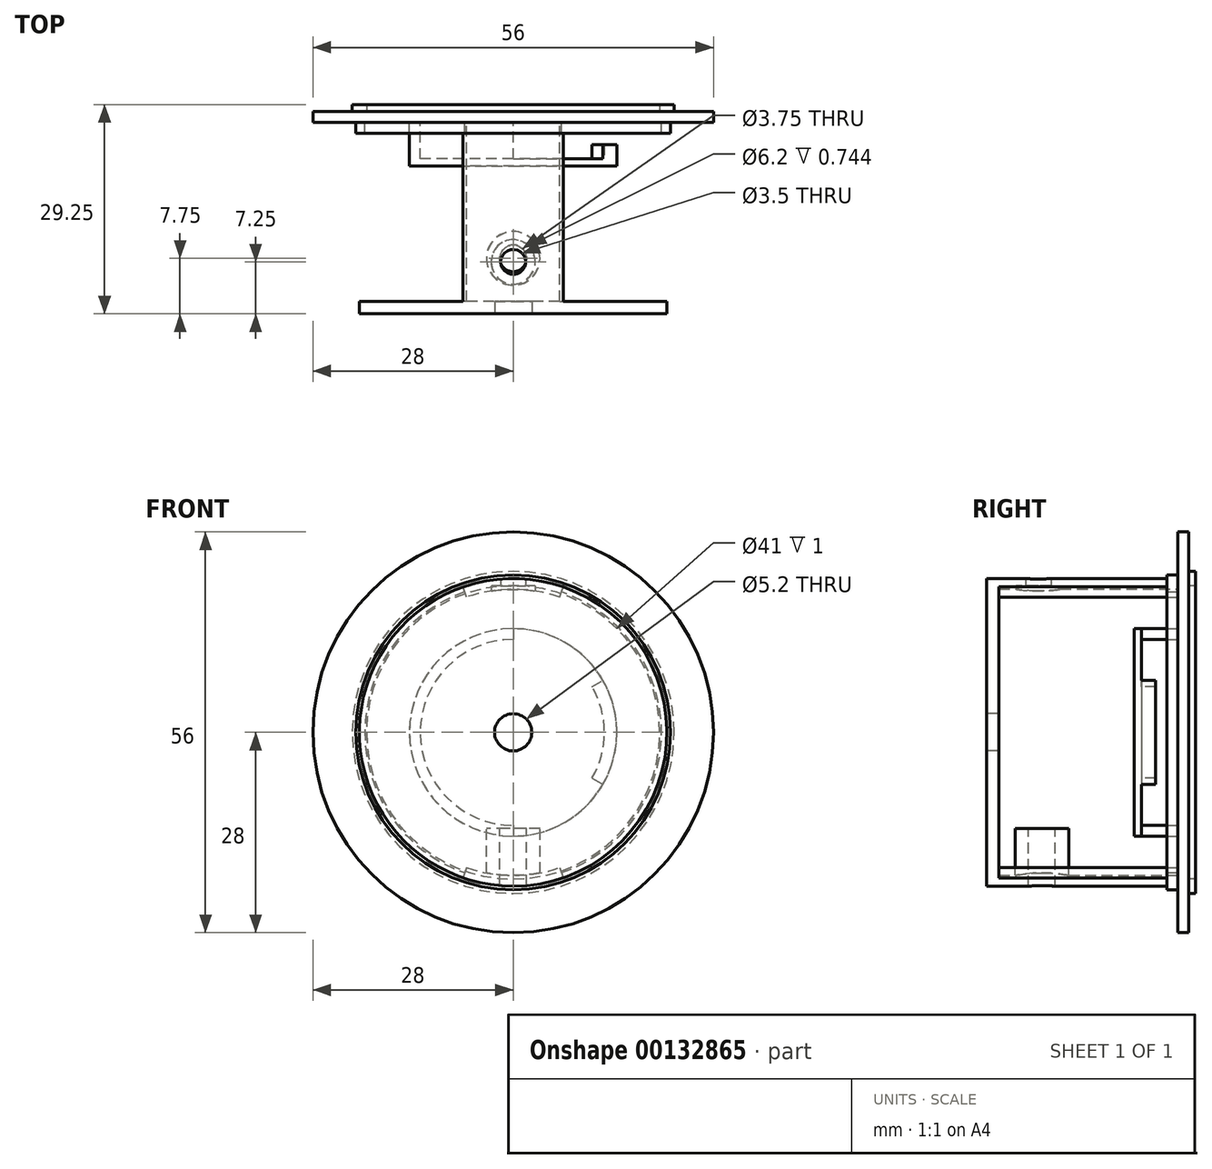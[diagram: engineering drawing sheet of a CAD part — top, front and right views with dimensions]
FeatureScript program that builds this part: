
annotation { "Feature Type Name" : "Feature", "Feature Type Description" : "" }
export const myFeature = defineFeature(function(context is Context, id is Id, definition is map)
    precondition{}
    {
        {
            var Q0;
            Q0=qCreatedBy(makeId("Front.planeOp"),FACE);
            var sketch = newSketch(context, id + "F0", { "sketchPlane" : qUnion([Q0])});
            skCircle(sketch, "E0", {"center": v(0, 0) * mm, "radius": 28 * mm});
            skSolve(sketch);
        }
        {
            var Q0;
            Q0=qSketchRegion(id+"F0",true);
            extrude(context, id + "F1", {"entities" : qUnion([Q0]), "depth" : 1.5 * mm});
        }
        {
            var Q0;
            Q0=makeQuery(id+"F1.opExtrude","CAP_FACE",FACE,{"disambiguationData":[OSD([sQuery(id+"F0.wireOp",EDGE,"E0")])],"isStart":false});
            var sketch = newSketch(context, id + "F2", { "sketchPlane" : qUnion([Q0])});
            skArc(sketch, "E1", {"start": v(0, 13) * mm, "mid": v(-13, 0) * mm, "end": v(0, -13) * mm});
            skArc(sketch, "E2", {"start": v(0, 14.5) * mm, "mid": v(-14.5, 0) * mm, "end": v(0, -14.5) * mm});
            skLineSegment(sketch, "E3", {"start": v(0, 14.5) * mm, "end": v(0, 13) * mm});
            skLineSegment(sketch, "E4.trimOffspring", {"start": v(0, -13) * mm, "end": v(0, -14.5) * mm});
            skSolve(sketch);
        }
        {
            var Q0;
            Q0=qSketchRegion(id+"F2",true);
            extrude(context, id + "F3", {"entities" : qUnion([Q0]), "operationType" : NewBodyOperationType.ADD, "depth" : 5.1 * mm});
        }
        {
            var Q0;
            {var subQ0=sQuery(id+"F0.wireOp",EDGE,"E0");Q0=makeQuery(id+"F3.boolean.opBoolean","SPLIT",FACE,{"disambiguationData":[TD([makeQuery(id+"F1.opExtrude","SWEPT_FACE",FACE,{"disambiguationData":[OSD([subQ0])]})])],"derivedFrom":makeQuery(id+"F1.opExtrude","CAP_FACE",FACE,{"disambiguationData":[OSD([subQ0])],"isStart":false})});}
            var sketch = newSketch(context, id + "F4", { "sketchPlane" : qUnion([Q0])});
            skArc(sketch, "E5", {"start": v(7, 20.33) * mm, "mid": v(0, 21.5) * mm, "end": v(-7, 20.33) * mm});
            skArc(sketch, "E6", {"start": v(6.51, 18.91) * mm, "mid": v(0, 20) * mm, "end": v(-6.51, 18.91) * mm});
            skLineSegment(sketch, "E7", {"start": v(0, 30.17) * mm, "end": v(0, -31.06) * mm, "construction": true});
            skLineSegment(sketch, "E8", {"start": v(-6.51, 18.91) * mm, "end": v(-7, 20.33) * mm});
            skLineSegment(sketch, "E9", {"start": v(6.51, 18.91) * mm, "end": v(7, 20.33) * mm});
            skArc(sketch, "E10.1.0", {"start": v(-6.51, -18.91) * mm, "mid": v(0, -20) * mm, "end": v(6.51, -18.91) * mm});
            skArc(sketch, "E10.1.1", {"start": v(-7, -20.33) * mm, "mid": v(0, -21.5) * mm, "end": v(7, -20.33) * mm});
            skLineSegment(sketch, "E10.1.2", {"start": v(-6.51, -18.91) * mm, "end": v(-7, -20.33) * mm});
            skLineSegment(sketch, "E10.1.3", {"start": v(6.51, -18.91) * mm, "end": v(7, -20.33) * mm});
            skSolve(sketch);
        }
        {
            var Q0;
            Q0=qSketchRegion(id+"F4",true);
            extrude(context, id + "F5", {"entities" : qUnion([Q0]), "operationType" : NewBodyOperationType.ADD, "depth" : 25 * mm});
        }
        {
            var Q0;
            Q0=makeQuery(id+"F5.opExtrude","CAP_FACE",FACE,{"disambiguationData":[OSD([sQuery(id+"F4.wireOp",EDGE,"E10.1.0"),sQuery(id+"F4.wireOp",EDGE,"E10.1.1"),sQuery(id+"F4.wireOp",EDGE,"E10.1.2"),sQuery(id+"F4.wireOp",EDGE,"E10.1.3")])],"isStart":false});
            var sketch = newSketch(context, id + "F6", { "sketchPlane" : qUnion([Q0])});
            skCircle(sketch, "E11", {"center": v(0, 0) * mm, "radius": 21.5 * mm});
            skSolve(sketch);
        }
        {
            var Q0;
            Q0=qSketchRegion(id+"F6",true);
            extrude(context, id + "F7", {"entities" : qUnion([Q0]), "operationType" : NewBodyOperationType.ADD, "depth" : 1.75 * mm});
        }
        {
            var Q0;
            Q0=makeQuery(id+"F7.opExtrude","CAP_FACE",FACE,{"disambiguationData":[OSD([sQuery(id+"F6.wireOp",EDGE,"E11")])],"isStart":false});
            var sketch = newSketch(context, id + "F8", { "sketchPlane" : qUnion([Q0])});
            skCircle(sketch, "E12", {"center": v(0, 0) * mm, "radius": 2.6 * mm});
            skSolve(sketch);
        }
        {
            var Q0;
            Q0=qSketchRegion(id+"F8",true);
            extrude(context, id + "F9", {"entities" : qUnion([Q0]), "operationType" : NewBodyOperationType.REMOVE, "oppositeDirection" : true, "depth" : 25 * mm});
        }
        {
            var Q0;
            Q0=qCreatedBy(makeId("Top.planeOp"),FACE);
            var sketch = newSketch(context, id + "F10", { "sketchPlane" : qUnion([Q0])});
            skCircle(sketch, "E13", {"center": v(0, -20.5) * mm, "radius": 1.98 * mm});
            skSolve(sketch);
        }
        {
            var Q0;
            Q0=qSketchRegion(id+"F10",true);
            extrude(context, id + "F11", {"entities" : qUnion([Q0]), "operationType" : NewBodyOperationType.REMOVE, "oppositeDirection" : true, "depth" : 30 * mm});
        }
        {
            var Q0;
            Q0=qCreatedBy(makeId("Top.planeOp"),FACE);
            var sketch = newSketch(context, id + "F12", { "sketchPlane" : qUnion([Q0])});
            skCircle(sketch, "E14", {"center": v(0, -20.5) * mm, "radius": 1.88 * mm});
            skCircle(sketch, "E15", {"center": v(0, -20.5) * mm, "radius": 3.75 * mm});
            skSolve(sketch);
        }
        {
            var Q0;
            Q0=qSketchRegion(id+"F12",true);
            var Q1;
            Q1=makeQuery(id+"F5.opExtrude","SWEPT_FACE",FACE,{"disambiguationData":[OSD([sQuery(id+"F4.wireOp",EDGE,"E10.1.1")])]});
            var Q2;
            Q2=makeQuery(id+"F1.opExtrude","SWEPT_BODY",BODY,{"disambiguationData":[OSD([sQuery(id+"F0.wireOp",EDGE,"E0")])]});
            var Q3;
            Q3=makeQuery(id+"F5.opExtrude","SWEPT_FACE",FACE,{"disambiguationData":[OSD([sQuery(id+"F4.wireOp",EDGE,"E6")])]});
            var Q4;
            Q4=makeQuery(id+"F1.opExtrude","SWEPT_BODY",BODY,{"disambiguationData":[OSD([sQuery(id+"F0.wireOp",EDGE,"E0")])]});
            extrude(context, id + "F13", {"entities" : qUnion([Q0]), "operationType" : NewBodyOperationType.ADD, "endBound" : BoundingType.UP_TO_SURFACE, "oppositeDirection" : true, "endBoundEntityFace" : qUnion([Q1]), "endBoundEntityBody" : qUnion([Q2]), "depth" : 25 * mm});
        }
        {
            var Q0;
            Q0=qCreatedBy(makeId("Right.planeOp"),FACE);
            var sketch = newSketch(context, id + "F14", { "sketchPlane" : qUnion([Q0])});
            skLineSegment(sketch, "E16.bottom", {"start": v(-10.25, 13.41) * mm, "end": v(-25.25, 13.41) * mm});
            skLineSegment(sketch, "E16.top", {"start": v(-10.25, -13.41) * mm, "end": v(-25.25, -13.41) * mm});
            skLineSegment(sketch, "E16.left", {"start": v(-10.25, 13.41) * mm, "end": v(-10.25, -13.41) * mm});
            skLineSegment(sketch, "E16.right", {"start": v(-25.25, 13.41) * mm, "end": v(-25.25, -13.41) * mm});
            skSolve(sketch);
        }
        {
            var Q0;
            Q0=qSketchRegion(id+"F14",true);
            extrude(context, id + "F15", {"entities" : qUnion([Q0]), "operationType" : NewBodyOperationType.REMOVE, "oppositeDirection" : true, "depth" : 25 * mm, "hasSecondDirection" : true, "secondDirectionOppositeDirection" : false, "secondDirectionDepth" : 25 * mm});
        }
        {
            var Q0;
            Q0=makeQuery(id+"F3.opExtrude","CAP_FACE",FACE,{"disambiguationData":[OSD([sQuery(id+"F2.wireOp",EDGE,"E1"),sQuery(id+"F2.wireOp",EDGE,"E2"),sQuery(id+"F2.wireOp",EDGE,"E3"),sQuery(id+"F2.wireOp",EDGE,"E4.trimOffspring")])],"isStart":false});
            var sketch = newSketch(context, id + "F16", { "sketchPlane" : qUnion([Q0])});
            skCircle(sketch, "E17", {"center": v(0, 0) * mm, "radius": 14.5 * mm});
            skSolve(sketch);
        }
        {
            var Q0;
            Q0=qSketchRegion(id+"F16",true);
            extrude(context, id + "F17", {"entities" : qUnion([Q0]), "operationType" : NewBodyOperationType.ADD, "depth" : 1 * mm});
        }
        {
            var Q0;
            Q0=makeQuery(id+"F17.opExtrude","CAP_FACE",FACE,{"disambiguationData":[OSD([sQuery(id+"F16.wireOp",EDGE,"E17")])],"isStart":true});
            var sketch = newSketch(context, id + "F18", { "sketchPlane" : qUnion([Q0])});
            skArc(sketch, "E18", {"start": v(-12.56, 7.25) * mm, "mid": v(-14.5, 0) * mm, "end": v(-12.56, -7.25) * mm});
            skArc(sketch, "E19", {"start": v(-11.04, 6.37) * mm, "mid": v(-12.75, 0) * mm, "end": v(-11.04, -6.38) * mm});
            skLineSegment(sketch, "E20", {"start": v(0, 14.5) * mm, "end": v(0, -14.5) * mm, "construction": true});
            skLineSegment(sketch, "E21", {"start": v(-11.04, 6.38) * mm, "end": v(-12.56, 7.25) * mm});
            skLineSegment(sketch, "E22", {"start": v(-11.04, -6.38) * mm, "end": v(-12.56, -7.25) * mm});
            skSolve(sketch);
        }
        {
            var Q0;
            Q0=qSketchRegion(id+"F18",true);
            extrude(context, id + "F19", {"entities" : qUnion([Q0]), "operationType" : NewBodyOperationType.ADD, "depth" : 2 * mm});
        }
        {
            var Q0;
            Q0=qCreatedBy(makeId("Top.planeOp"),FACE);
            cPlane(context, id + "F20", {"entities" : qUnion([Q0]), "cplaneType" : CPlaneType.OFFSET, "offset" : 15 * mm, "width" : 150 * mm, "height" : 150 * mm});
        }
        {
            var Q0;
            Q0=makeQuery(id+"F1.opExtrude","CAP_FACE",FACE,{"disambiguationData":[OSD([sQuery(id+"F0.wireOp",EDGE,"E0")])],"isStart":true});
            var sketch = newSketch(context, id + "F21", { "sketchPlane" : qUnion([Q0])});
            skCircle(sketch, "E23", {"center": v(0, 0) * mm, "radius": 22.5 * mm});
            skCircle(sketch, "E24", {"center": v(0, 0) * mm, "radius": 20.5 * mm});
            skSolve(sketch);
        }
        {
            var Q0;
            Q0=qSketchRegion(id+"F21",true);
            extrude(context, id + "F22", {"entities" : qUnion([Q0]), "operationType" : NewBodyOperationType.ADD, "depth" : 1 * mm});
        }
        {
            var Q0;
            Q0=makeQuery(id+"F1.opExtrude","CAP_FACE",FACE,{"disambiguationData":[OSD([sQuery(id+"F0.wireOp",EDGE,"E0")])],"isStart":false});
            var sketch = newSketch(context, id + "F23", { "sketchPlane" : qUnion([Q0])});
            skCircle(sketch, "E25", {"center": v(0, 0) * mm, "radius": 22 * mm});
            skCircle(sketch, "E26", {"center": v(0, 0) * mm, "radius": 20.75 * mm});
            skSolve(sketch);
        }
        {
            var Q0;
            Q0=qSketchRegion(id+"F23",true);
            extrude(context, id + "F24", {"entities" : qUnion([Q0]), "operationType" : NewBodyOperationType.ADD, "depth" : 1.5 * mm});
        }
        {
            var Q0;
            Q0=qCreatedBy(id+"F20.planeOp",FACE);
            var sketch = newSketch(context, id + "F25", { "sketchPlane" : qUnion([Q0])});
            skCircle(sketch, "E27", {"center": v(0, -21) * mm, "radius": 3.1 * mm});
            skSolve(sketch);
        }
        {
            var Q0;
            Q0=qSketchRegion(id+"F25",true);
            extrude(context, id + "F26", {"entities" : qUnion([Q0]), "operationType" : NewBodyOperationType.REMOVE, "depth" : 5.5 * mm});
        }
        {
            var Q0;
            Q0=makeQuery(id+"F26.boolean.opBoolean","COPY",FACE,{"derivedFrom":makeQuery(id+"F26.opExtrude","CAP_FACE",FACE,{"disambiguationData":[OSD([sQuery(id+"F25.wireOp",EDGE,"E27")])],"isStart":false})});
            var sketch = newSketch(context, id + "F27", { "sketchPlane" : qUnion([Q0])});
            skCircle(sketch, "E28", {"center": v(0, 21) * mm, "radius": 1.75 * mm});
            skSolve(sketch);
        }
        {
            var Q0;
            Q0=qSketchRegion(id+"F27",true);
            var Q1;
            {var subQ0=sQuery(id+"F6.wireOp",EDGE,"E11");var subQ1=sQuery(id+"F4.wireOp",EDGE,"E10.1.1");var subQ2=sQuery(id+"F4.wireOp",EDGE,"E5");Q1=makeQuery(id+"F13.boolean.opBoolean","MERGE",FACE,{"derivedFrom":[makeQuery(id+"F7.boolean.opBoolean","MERGE",FACE,{"derivedFrom":[makeQuery(id+"F5.opExtrude","SWEPT_FACE",FACE,{"disambiguationData":[OSD([subQ2])]}),makeQuery(id+"F5.opExtrude","SWEPT_FACE",FACE,{"disambiguationData":[OSD([subQ1])]}),makeQuery(id+"F7.opExtrude","SWEPT_FACE",FACE,{"disambiguationData":[OSD([subQ0])]})]}),makeQuery(id+"F13.opExtrude","CAP_FACE",FACE,{"disambiguationData":[OSD([subQ2,subQ1,subQ0])],"isStart":false})]});}
            extrude(context, id + "F28", {"entities" : qUnion([Q0]), "operationType" : NewBodyOperationType.REMOVE, "endBound" : BoundingType.UP_TO_SURFACE, "oppositeDirection" : true, "endBoundEntityFace" : qUnion([Q1]), "depth" : 25 * mm});
        }
        {
            var Q0;
            {var subQ0=sQuery(id+"F0.wireOp",EDGE,"E0");Q0=makeQuery(id+"F24.boolean.opBoolean","SPLIT",FACE,{"disambiguationData":[TD([makeQuery(id+"F1.opExtrude","SWEPT_FACE",FACE,{"disambiguationData":[OSD([subQ0])]})])],"derivedFrom":makeQuery(id+"F1.opExtrude","CAP_FACE",FACE,{"disambiguationData":[OSD([subQ0])],"isStart":false})});}
            var sketch = newSketch(context, id + "F29", { "sketchPlane" : qUnion([Q0])});
            skCircle(sketch, "E29", {"center": v(0, 0) * mm, "radius": 29 * mm});
            skCircle(sketch, "E30", {"center": v(0, 0) * mm, "radius": 30 * mm});
            skSolve(sketch);
        }
        {
            var Q0;
            Q0=qSketchRegion(id+"F29",true);
            extrude(context, id + "F30", {"entities" : qUnion([Q0]), "operationType" : NewBodyOperationType.REMOVE, "depth" : 25 * mm});
        }
    });
